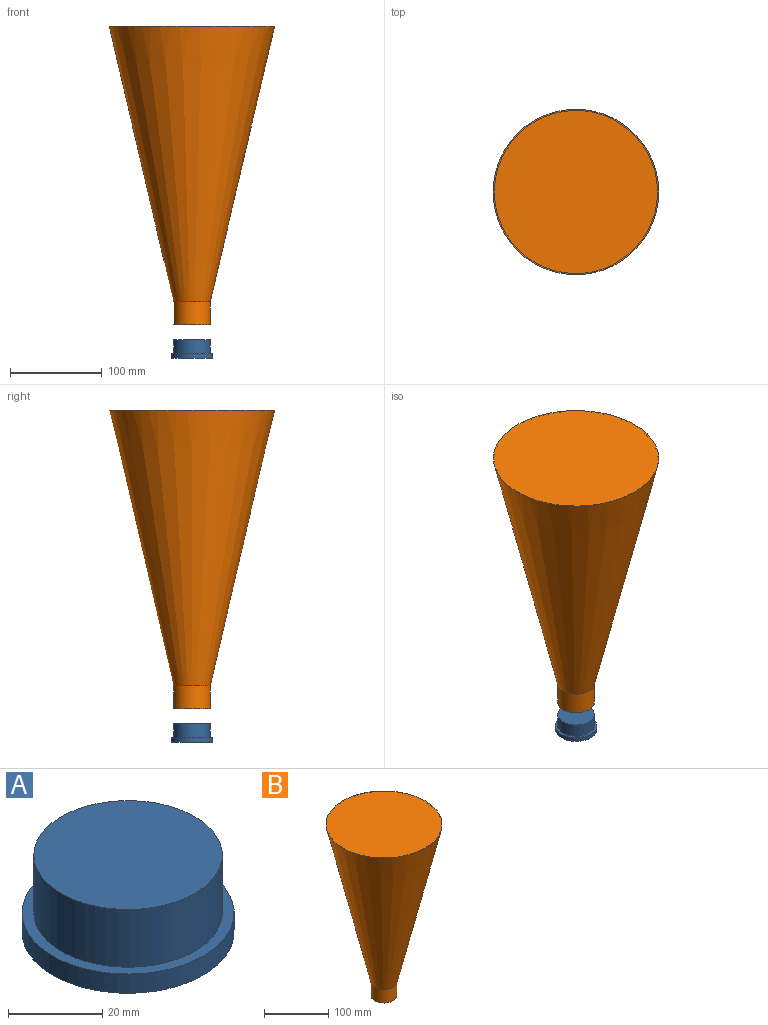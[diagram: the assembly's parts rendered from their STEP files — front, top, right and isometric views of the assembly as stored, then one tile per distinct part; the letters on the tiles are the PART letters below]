
ASSEMBLY  parts=2 mates=1
PART A: 5 faces, bbox 45x45x20 mm
  f0: cylinder r=20mm len=40mm, axis (0,0,-1), area 1885mm2, adj f1,f3
  f1: plane 40x40mm, normal (0,0,1), area 1256.6mm2, adj f0
  f2: cylinder r=22.5mm len=45mm, axis (0,0,-1), area 706.9mm2, adj f3,f4
  f3: plane 45x45mm, normal (0,0,1), area 333.8mm2, adj f0,f2
  f4: plane 45x45mm, normal (0,0,-1), area 1590.4mm2, adj f2
PART B: 8 faces, bbox 180x180x325 mm
  f0: cylinder r=19mm len=38mm, axis (0,0,-1), area 3103.9mm2, adj f2,f5
  f1: plane 177.48x177.48mm, normal (0,0,-1), area 24739.3mm2, adj f3
  f2: plane 38.41x38.41mm, normal (0,0,1), area 24.8mm2, adj f0,f3
  f3: cone r=89.03mm half-angle=13.1deg, axis (0,0,1), area 103773.3mm2, adj f1,f2
  f4: cylinder r=20mm len=40mm, axis (0,0,1), area 3141.6mm2, adj f5,f7
  f5: plane 40x40mm, normal (0,0,-1), area 122.5mm2, adj f0,f4
  f6: plane 180x180mm, normal (0,0,1), area 25446.9mm2, adj f7
  f7: cone r=90mm half-angle=13.1deg, axis (0,0,1), area 106457.4mm2, adj f4,f6
PLACE A rot(axis=(0,0,-1),116.3deg) t=(-120.64,3.51,-88.95)mm
PLACE B t=(-120.64,3.51,-27.76)mm fixed
MATE cylindrical A.f0 <-> B.f4  axis (0,0,-1) through (-120.64,3.51,-76.45)mm
